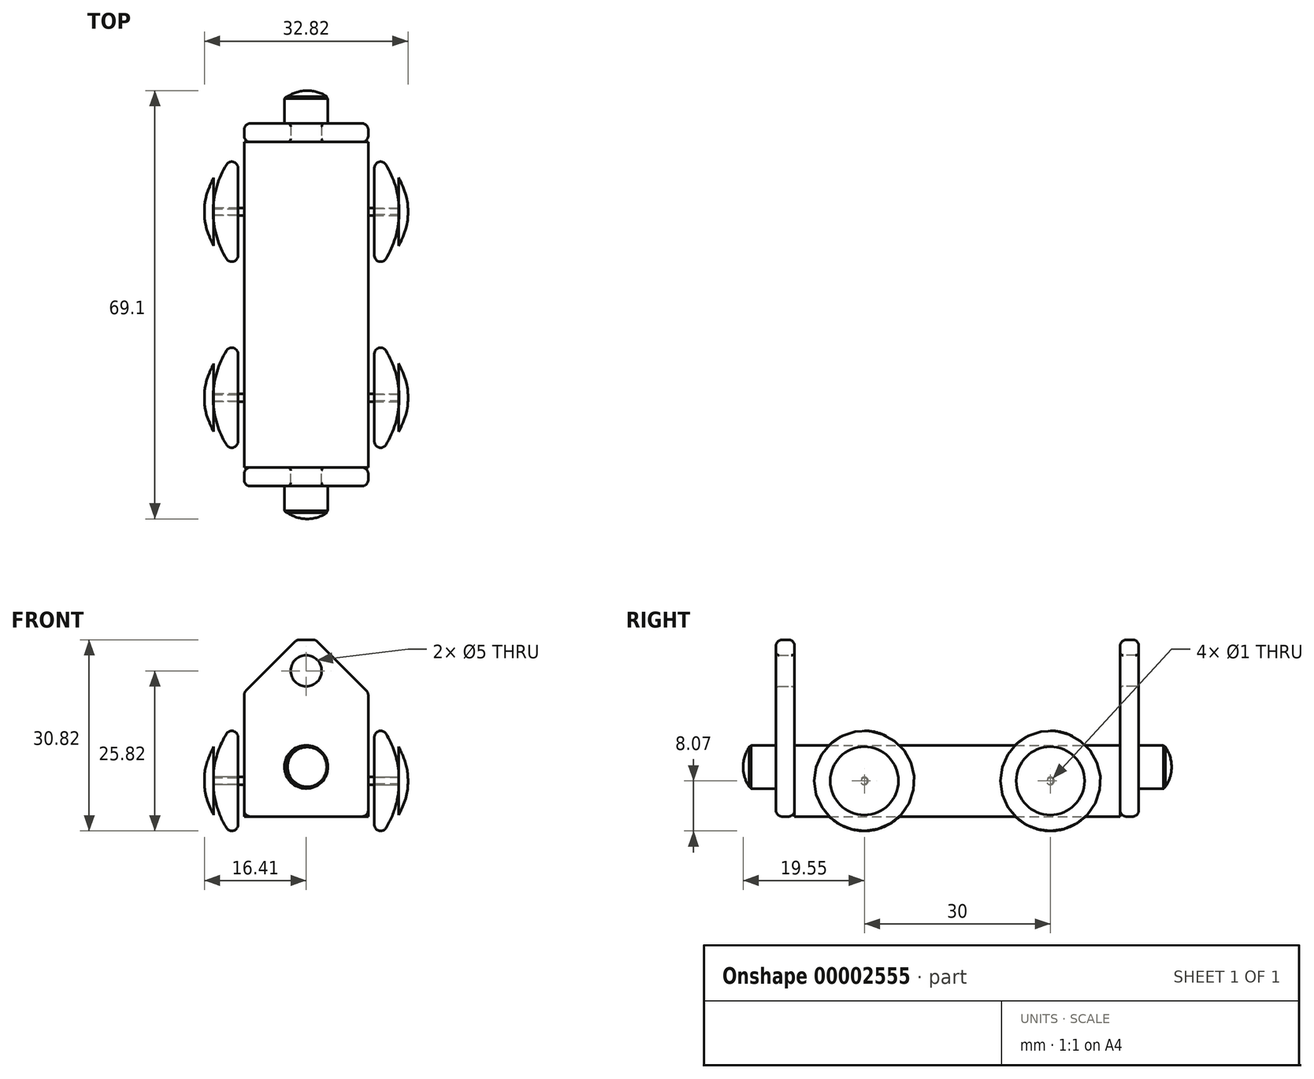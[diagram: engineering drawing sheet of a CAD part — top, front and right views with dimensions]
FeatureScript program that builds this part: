
annotation { "Feature Type Name" : "Feature", "Feature Type Description" : "" }
export const myFeature = defineFeature(function(context is Context, id is Id, definition is map)
    precondition{}
    {
        {
            var Q0;
            Q0=qCreatedBy(makeId("Top.planeOp"),FACE);
            var sketch = newSketch(context, id + "F0", { "sketchPlane" : qUnion([Q0])});
            skLineSegment(sketch, "E0.bottom", {"start": v(0, 0) * mm, "end": v(20, 0) * mm});
            skLineSegment(sketch, "E0.top", {"start": v(0, 52.5) * mm, "end": v(20, 52.5) * mm});
            skLineSegment(sketch, "E0.left", {"start": v(0, 0) * mm, "end": v(0, 52.5) * mm});
            skLineSegment(sketch, "E0.right", {"start": v(20, 0) * mm, "end": v(20, 52.5) * mm});
            skSolve(sketch);
        }
        {
            var Q0;
            Q0=makeQuery(id+"F0.imprint","IMPRINT",FACE,{"disambiguationData":[TD([[makeQuery(id+"F0.imprint","IMPRINT",EDGE,{"derivedFrom":sQuery(id+"F0.wireOp",EDGE,"E0.bottom")}),1.0]])]});
            extrude(context, id + "F1", {"entities" : qUnion([Q0]), "depth" : 11.5 * mm});
        }
        {
            var Q0;
            Q0=makeQuery(id+"F1.opExtrude","SWEPT_FACE",FACE,{"disambiguationData":[OSD([sQuery(id+"F0.wireOp",EDGE,"E0.bottom")])]});
            var sketch = newSketch(context, id + "F2", { "sketchPlane" : qUnion([Q0])});
            skLineSegment(sketch, "E1.bottom", {"start": v(1, 0) * mm, "end": v(19, 0) * mm});
            skLineSegment(sketch, "E1.top", {"start": v(0, 20) * mm, "end": v(20, 20) * mm});
            skLineSegment(sketch, "E1.left", {"start": v(0, 1) * mm, "end": v(0, 19.59) * mm});
            skLineSegment(sketch, "E1.right", {"start": v(20, 1) * mm, "end": v(20, 19.59) * mm});
            skLineSegment(sketch, "E2", {"start": v(0.3, 20.3) * mm, "end": v(8.2, 28.2) * mm});
            skLineSegment(sketch, "E3", {"start": v(8.91, 28.5) * mm, "end": v(10, 28.5) * mm});
            skLineSegment(sketch, "E4", {"start": v(10, 20) * mm, "end": v(10, 28.5) * mm, "construction": true});
            skLineSegment(sketch, "E5.0.MirrorCS", {"start": v(19.7, 20.3) * mm, "end": v(11.8, 28.2) * mm});
            skLineSegment(sketch, "E6.0.MirrorCS", {"start": v(11.09, 28.5) * mm, "end": v(10, 28.5) * mm});
            skPoint(sketch, "E7.visualSharp", {"position": v(0, 0) * mm});
            skArc(sketch, "E7.filletArc", {"start": v(0, 1) * mm, "mid": v(0.3, 0.3) * mm, "end": v(1, 0) * mm});
            skPoint(sketch, "E8.visualSharp", {"position": v(20, 0) * mm});
            skArc(sketch, "E8.filletArc", {"start": v(19, 0) * mm, "mid": v(19.7, 0.3) * mm, "end": v(20, 1) * mm});
            skPoint(sketch, "E9.visualSharp", {"position": v(20, 20) * mm});
            skArc(sketch, "E9.filletArc", {"start": v(20, 19.59) * mm, "mid": v(19.92, 19.97) * mm, "end": v(19.7, 20.3) * mm});
            skPoint(sketch, "E10.visualSharp", {"position": v(11.5, 28.5) * mm});
            skArc(sketch, "E10.filletArc", {"start": v(11.8, 28.2) * mm, "mid": v(11.47, 28.42) * mm, "end": v(11.09, 28.5) * mm});
            skPoint(sketch, "E11.visualSharp", {"position": v(8.5, 28.5) * mm});
            skArc(sketch, "E11.filletArc", {"start": v(8.91, 28.5) * mm, "mid": v(8.53, 28.42) * mm, "end": v(8.2, 28.2) * mm});
            skPoint(sketch, "E12.visualSharp", {"position": v(0, 20) * mm});
            skArc(sketch, "E12.filletArc", {"start": v(0.3, 20.3) * mm, "mid": v(0.08, 19.97) * mm, "end": v(0, 19.59) * mm});
            skCircle(sketch, "E13", {"center": v(10, 23.5) * mm, "radius": 2.5 * mm});
            skSolve(sketch);
        }
        {
            var Q0;
            {var subQ0=makeQuery(id+"F1.opExtrude","CAP_EDGE",EDGE,{"disambiguationData":[OSD([sQuery(id+"F0.wireOp",EDGE,"E0.bottom")])],"isStart":false});Q0=makeQuery(id+"F2.imprint","IMPRINT",FACE,{"disambiguationData":[TD([[makeQuery(id+"F2.imprint","IMPRINT",EDGE,{"derivedFrom":subQ0}),1.0]])]});}
            var Q1;
            Q1=makeQuery(id+"F2.imprint","IMPRINT",FACE,{"disambiguationData":[TD([[makeQuery(id+"F2.imprint","IMPRINT",EDGE,{"derivedFrom":sQuery(id+"F2.wireOp",EDGE,"E1.bottom")}),1.0]])]});
            var Q2;
            {var subQ3=sQuery(id+"F2.wireOp",EDGE,"E2");Q2=makeQuery(id+"F2.imprint","IMPRINT",FACE,{"disambiguationData":[TD([[makeQuery(id+"F2.imprint","IMPRINT",EDGE,{"derivedFrom":subQ3}),-1.0]])]});}
            extrude(context, id + "F3", {"entities" : qUnion([Q0, Q1, Q2]), "depth" : 3 * mm});
        }
        {
            var Q0;
            Q0=makeQuery(id+"F3.opExtrude","CAP_EDGE",EDGE,{"disambiguationData":[OSD([sQuery(id+"F2.wireOp",EDGE,"E2")])],"isStart":false});
            var Q1;
            Q1=makeQuery(id+"F3.opExtrude","SWEPT_FACE",FACE,{"disambiguationData":[OSD([sQuery(id+"F2.wireOp",EDGE,"E5.0.MirrorCS")])]});
            fillet(context, id + "F4", {"entities" : qUnion([Q0, Q1]), "radius" : 1 * mm, "tangentPropagation" : true, "allowEdgeOverflow" : false});
        }
        {
            var Q0;
            Q0=makeQuery(id+"F3.opExtrude","CAP_EDGE",EDGE,{"disambiguationData":[OSD([sQuery(id+"F2.wireOp",EDGE,"E13")])],"isStart":true});
            var Q1;
            Q1=makeQuery(id+"F3.opExtrude","CAP_EDGE",EDGE,{"disambiguationData":[OSD([sQuery(id+"F2.wireOp",EDGE,"E13")])],"isStart":false});
            fillet(context, id + "F5", {"entities" : qUnion([Q0, Q1]), "radius" : 0.5 * mm, "tangentPropagation" : true, "allowEdgeOverflow" : false});
        }
        {
            var Q0;
            Q0=makeQuery(id+"F1.opExtrude","SWEPT_FACE",FACE,{"disambiguationData":[OSD([sQuery(id+"F0.wireOp",EDGE,"E0.top")])]});
            var Q1;
            Q1=makeQuery(id+"F3.opExtrude","CAP_FACE",FACE,{"disambiguationData":[OSD([sQuery(id+"F2.wireOp",EDGE,"E1.bottom"),sQuery(id+"F2.wireOp",EDGE,"E1.left"),sQuery(id+"F2.wireOp",EDGE,"E1.right"),sQuery(id+"F2.wireOp",EDGE,"E2"),sQuery(id+"F2.wireOp",EDGE,"E5.0.MirrorCS"),sQuery(id+"F2.wireOp",EDGE,"E6.0.MirrorCS"),sQuery(id+"F2.wireOp",EDGE,"E7.filletArc"),sQuery(id+"F2.wireOp",EDGE,"E8.filletArc"),sQuery(id+"F2.wireOp",EDGE,"E9.filletArc"),sQuery(id+"F2.wireOp",EDGE,"E10.filletArc"),sQuery(id+"F2.wireOp",EDGE,"E11.filletArc"),sQuery(id+"F2.wireOp",EDGE,"E12.filletArc"),sQuery(id+"F2.wireOp",EDGE,"E13")])],"isStart":true});
            cPlane(context, id + "F6", {"entities" : qUnion([Q0, Q1]), "cplaneType" : CPlaneType.MID_PLANE, "offset" : 150 * mm, "width" : 150 * mm, "height" : 150 * mm});
        }
        {
            var Q0;
            Q0=makeQuery(id+"F3.opExtrude","SWEPT_BODY",BODY,{"disambiguationData":[OSD([sQuery(id+"F2.wireOp",EDGE,"E1.bottom"),sQuery(id+"F2.wireOp",EDGE,"E1.left"),sQuery(id+"F2.wireOp",EDGE,"E1.right"),sQuery(id+"F2.wireOp",EDGE,"E2"),sQuery(id+"F2.wireOp",EDGE,"E5.0.MirrorCS"),sQuery(id+"F2.wireOp",EDGE,"E6.0.MirrorCS"),sQuery(id+"F2.wireOp",EDGE,"E7.filletArc"),sQuery(id+"F2.wireOp",EDGE,"E8.filletArc"),sQuery(id+"F2.wireOp",EDGE,"E9.filletArc"),sQuery(id+"F2.wireOp",EDGE,"E10.filletArc"),sQuery(id+"F2.wireOp",EDGE,"E11.filletArc"),sQuery(id+"F2.wireOp",EDGE,"E12.filletArc"),sQuery(id+"F2.wireOp",EDGE,"E13")])]});
            var Q1;
            Q1=qCreatedBy(id+"F6.planeOp",FACE);
            mirror(context, id + "F7", {"entities" : qUnion([Q0]), "mirrorPlane" : qUnion([Q1])});
        }
        {
            var Q0;
            Q0=makeQuery(id+"F3.opExtrude","CAP_FACE",FACE,{"disambiguationData":[OSD([sQuery(id+"F2.wireOp",EDGE,"E1.bottom"),sQuery(id+"F2.wireOp",EDGE,"E1.left"),sQuery(id+"F2.wireOp",EDGE,"E1.right"),sQuery(id+"F2.wireOp",EDGE,"E2"),sQuery(id+"F2.wireOp",EDGE,"E5.0.MirrorCS"),sQuery(id+"F2.wireOp",EDGE,"E6.0.MirrorCS"),sQuery(id+"F2.wireOp",EDGE,"E7.filletArc"),sQuery(id+"F2.wireOp",EDGE,"E8.filletArc"),sQuery(id+"F2.wireOp",EDGE,"E9.filletArc"),sQuery(id+"F2.wireOp",EDGE,"E10.filletArc"),sQuery(id+"F2.wireOp",EDGE,"E11.filletArc"),sQuery(id+"F2.wireOp",EDGE,"E12.filletArc"),sQuery(id+"F2.wireOp",EDGE,"E13")])],"isStart":false});
            var sketch = newSketch(context, id + "F8", { "sketchPlane" : qUnion([Q0])});
            skLineSegment(sketch, "E14", {"start": v(10, 1) * mm, "end": v(10, 8) * mm, "construction": true});
            skCircle(sketch, "E15", {"center": v(10, 8) * mm, "radius": 3.5 * mm});
            skSolve(sketch);
        }
        {
            var Q0;
            Q0=makeQuery(id+"F8.imprint","IMPRINT",FACE,{"disambiguationData":[TD([[makeQuery(id+"F8.imprint","IMPRINT",EDGE,{"derivedFrom":sQuery(id+"F8.wireOp",EDGE,"E15")}),1.0]])]});
            extrude(context, id + "F9", {"entities" : qUnion([Q0]), "depth" : 4.3 * mm});
        }
        {
            var Q0;
            Q0=makeQuery(id+"F9.opExtrude","CAP_FACE",FACE,{"disambiguationData":[OSD([sQuery(id+"F8.wireOp",EDGE,"E15")])],"isStart":false});
            chamfer(context, id + "F10", {"entities" : qUnion([Q0]), "width" : 0.3 * mm, "tangentPropagation" : true});
        }
        {
            var Q0;
            Q0=makeQuery(id+"F9.opExtrude","CAP_FACE",FACE,{"disambiguationData":[OSD([sQuery(id+"F8.wireOp",EDGE,"E15")])],"isStart":false});
            var sketch = newSketch(context, id + "F11", { "sketchPlane" : qUnion([Q0])});
            skLineSegment(sketch, "E16", {"start": v(10.17, 11.2) * mm, "end": v(10.17, 4.8) * mm, "construction": true});
            skSolve(sketch);
        }
        {
            var Q0;
            Q0=sQuery(id+"F11.wireOp",EDGE,"E16");
            cPlane(context, id + "F12", {"entities" : qUnion([Q0]), "cplaneType" : CPlaneType.LINE_ANGLE, "offset" : 150 * mm, "angle" : 0 * degree, "width" : 150 * mm, "height" : 150 * mm});
        }
        {
            var Q0;
            Q0=qCreatedBy(id+"F12.planeOp",FACE);
            var sketch = newSketch(context, id + "F13", { "sketchPlane" : qUnion([Q0])});
            skArc(sketch, "E17", {"start": v(8.3, 8) * mm, "mid": v(8.04, 9.67) * mm, "end": v(7.3, 11.2) * mm});
            skPoint(sketch, "E17.first.point", {"position": v(7.3, 11.2) * mm});
            skPoint(sketch, "E17.second.point", {"position": v(7.3, 4.8) * mm});
            skPoint(sketch, "E17.third.point", {"position": v(-2.88, 7.11) * mm});
            skLineSegment(sketch, "E18.0", {"start": v(7.3, 11.2) * mm, "end": v(7.3, 4.8) * mm});
            skLineSegment(sketch, "E19", {"start": v(8.3, 8) * mm, "end": v(7.3, 8) * mm});
            skSolve(sketch);
        }
        {
            var Q0;
            {var subQ2=sQuery(id+"F13.wireOp",EDGE,"E17");Q0=makeQuery(id+"F13.imprint","IMPRINT",FACE,{"disambiguationData":[TD([[makeQuery(id+"F13.imprint","IMPRINT",EDGE,{"derivedFrom":subQ2}),1.0]])]});}
            var Q1;
            Q1=sQuery(id+"F13.wireOp",EDGE,"E19");
            revolve(context, id + "F14", {"entities" : qUnion([Q0]), "axis" : qUnion([Q1]), "revolveType" : RevolveType.FULL});
        }
        {
            var Q0;
            Q0=makeQuery(id+"F9.opExtrude","SWEPT_BODY",BODY,{"disambiguationData":[OSD([sQuery(id+"F8.wireOp",EDGE,"E15")])]});
            var Q1;
            Q1=makeQuery(id+"F14.opRevolve","SWEPT_BODY",BODY,{"disambiguationData":[OSD([sQuery(id+"F13.wireOp",EDGE,"E17"),sQuery(id+"F13.wireOp",EDGE,"E18.0"),sQuery(id+"F13.wireOp",EDGE,"E19")])]});
            var Q2;
            Q2=qCreatedBy(id+"F6.planeOp",FACE);
            mirror(context, id + "F15", {"entities" : qUnion([Q0, Q1]), "mirrorPlane" : qUnion([Q2])});
        }
        {
            var Q0;
            Q0=qCreatedBy(id+"F6.planeOp",FACE);
            var sketch = newSketch(context, id + "F16", { "sketchPlane" : qUnion([Q0])});
            skArc(sketch, "E20", {"start": v(2.85, -1.84) * mm, "mid": v(4.45, 1.8) * mm, "end": v(5, 5.75) * mm});
            skPoint(sketch, "E20.first.point", {"position": v(1, 15.75) * mm});
            skPoint(sketch, "E20.second.point", {"position": v(1, -4.25) * mm});
            skLineSegment(sketch, "E21.0", {"start": v(0, 11.5) * mm, "end": v(0, 0) * mm, "construction": true});
            skLineSegment(sketch, "E22", {"start": v(0, 5.75) * mm, "end": v(-31.51, 5.75) * mm, "construction": true});
            skLineSegment(sketch, "E23", {"start": v(1, 5.75) * mm, "end": v(1, -1.32) * mm});
            skArc(sketch, "E24.filletArc", {"start": v(1, -1.32) * mm, "mid": v(1.73, -2.28) * mm, "end": v(2.85, -1.84) * mm});
            skLineSegment(sketch, "E25", {"start": v(1, 5.75) * mm, "end": v(5, 5.75) * mm, "construction": true});
            skLineSegment(sketch, "E26", {"start": v(1, 5.25) * mm, "end": v(5, 5.25) * mm});
            skSolve(sketch);
        }
        {
            var Q0;
            Q0=qCreatedBy(id+"F6.planeOp",FACE);
            cPlane(context, id + "F17", {"entities" : qUnion([Q0]), "cplaneType" : CPlaneType.OFFSET, "offset" : 15 * mm, "width" : 150 * mm, "height" : 150 * mm});
        }
        {
            var Q0;
            Q0=qCreatedBy(id+"F17.planeOp",FACE);
            var sketch = newSketch(context, id + "F18", { "sketchPlane" : qUnion([Q0])});
            skLineSegment(sketch, "E27.0", {"start": v(1, 5.75) * mm, "end": v(1, -1.32) * mm});
            skArc(sketch, "E28.0", {"start": v(1, -1.32) * mm, "mid": v(1.73, -2.28) * mm, "end": v(2.85, -1.84) * mm});
            skArc(sketch, "E29.0", {"start": v(2.85, -1.84) * mm, "mid": v(4.45, 1.8) * mm, "end": v(5, 5.75) * mm});
            skLineSegment(sketch, "E30.0", {"start": v(1, 5.25) * mm, "end": v(5, 5.25) * mm});
            skLineSegment(sketch, "E31.0", {"start": v(1, 5.75) * mm, "end": v(5, 5.75) * mm, "construction": true});
            skSolve(sketch);
        }
        {
            var Q0;
            {var subQ2=sQuery(id+"F18.wireOp",EDGE,"E28.0");Q0=makeQuery(id+"F18.imprint","IMPRINT",FACE,{"disambiguationData":[TD([[makeQuery(id+"F18.imprint","IMPRINT",EDGE,{"derivedFrom":subQ2}),1.0]])]});}
            var Q1;
            Q1=sQuery(id+"F18.wireOp",EDGE,"E31.0");
            revolve(context, id + "F19", {"entities" : qUnion([Q0]), "axis" : qUnion([Q1]), "revolveType" : RevolveType.FULL});
        }
        {
            var Q0;
            Q0=qCreatedBy(id+"F17.planeOp",FACE);
            var sketch = newSketch(context, id + "F20", { "sketchPlane" : qUnion([Q0])});
            skLineSegment(sketch, "E32", {"start": v(0, 5.13) * mm, "end": v(4.91, 5.13) * mm});
            skLineSegment(sketch, "E33", {"start": v(4.91, 5.13) * mm, "end": v(4.91, 0.25) * mm});
            skFitSpline(sketch, "E34", {"points": [v(4.91, 0.25) * mm, v(6.17, 3.4) * mm, v(6.4, 5.75) * mm], "startDerivative": vector(0.77, 1.16) * mm, "endDerivative": vector(0.03, 2.6) * mm});
            skLineSegment(sketch, "E35.0", {"start": v(1, 5.75) * mm, "end": v(6.4, 5.75) * mm, "construction": true});
            skPoint(sketch, "E36.orphan", {"position": v(5, 5.75) * mm});
            skLineSegment(sketch, "E37", {"start": v(6.4, 5.75) * mm, "end": v(0, 5.75) * mm});
            skLineSegment(sketch, "E38", {"start": v(0, 5.75) * mm, "end": v(0, 5.13) * mm});
            skSolve(sketch);
        }
        {
            var Q0;
            Q0=makeQuery(id+"F20.imprint","IMPRINT",FACE,{"disambiguationData":[TD([[makeQuery(id+"F20.imprint","IMPRINT",EDGE,{"derivedFrom":sQuery(id+"F20.wireOp",EDGE,"E32")}),1.0]])]});
            var Q1;
            Q1=sQuery(id+"F20.wireOp",EDGE,"E37");
            revolve(context, id + "F21", {"entities" : qUnion([Q0]), "axis" : qUnion([Q1]), "revolveType" : RevolveType.FULL});
        }
        {
            var Q0;
            Q0=makeQuery(id+"F21.opRevolve","SWEPT_BODY",BODY,{"disambiguationData":[OSD([sQuery(id+"F20.wireOp",EDGE,"E32"),sQuery(id+"F20.wireOp",EDGE,"E33"),sQuery(id+"F20.wireOp",EDGE,"E34"),sQuery(id+"F20.wireOp",EDGE,"E37"),sQuery(id+"F20.wireOp",EDGE,"E38")])]});
            var Q1;
            Q1=makeQuery(id+"F19.opRevolve","SWEPT_BODY",BODY,{"disambiguationData":[OSD([sQuery(id+"F18.wireOp",EDGE,"E27.0"),sQuery(id+"F18.wireOp",EDGE,"E28.0"),sQuery(id+"F18.wireOp",EDGE,"E29.0"),sQuery(id+"F18.wireOp",EDGE,"E30.0")])]});
            var Q2;
            Q2=qCreatedBy(id+"F6.planeOp",FACE);
            mirror(context, id + "F22", {"entities" : qUnion([Q0, Q1]), "mirrorPlane" : qUnion([Q2])});
        }
        {
            var Q0;
            Q0=makeQuery(id+"F1.opExtrude","SWEPT_FACE",FACE,{"disambiguationData":[OSD([sQuery(id+"F0.wireOp",EDGE,"E0.left")])]});
            var Q1;
            Q1=makeQuery(id+"F1.opExtrude","SWEPT_FACE",FACE,{"disambiguationData":[OSD([sQuery(id+"F0.wireOp",EDGE,"E0.right")])]});
            cPlane(context, id + "F23", {"entities" : qUnion([Q0, Q1]), "cplaneType" : CPlaneType.MID_PLANE, "offset" : 150 * mm, "width" : 150 * mm, "height" : 150 * mm});
        }
        {
            var Q0;
            Q0=makeQuery(id+"F22.opPattern","COPY",BODY,{"derivedFrom":makeQuery(id+"F21.opRevolve","SWEPT_BODY",BODY,{"disambiguationData":[OSD([sQuery(id+"F20.wireOp",EDGE,"E32"),sQuery(id+"F20.wireOp",EDGE,"E33"),sQuery(id+"F20.wireOp",EDGE,"E34"),sQuery(id+"F20.wireOp",EDGE,"E37"),sQuery(id+"F20.wireOp",EDGE,"E38")])]}),"instanceName":"1"});
            var Q1;
            Q1=makeQuery(id+"F19.opRevolve","SWEPT_BODY",BODY,{"disambiguationData":[OSD([sQuery(id+"F18.wireOp",EDGE,"E27.0"),sQuery(id+"F18.wireOp",EDGE,"E28.0"),sQuery(id+"F18.wireOp",EDGE,"E29.0"),sQuery(id+"F18.wireOp",EDGE,"E30.0")])]});
            var Q2;
            Q2=makeQuery(id+"F22.opPattern","COPY",BODY,{"derivedFrom":makeQuery(id+"F19.opRevolve","SWEPT_BODY",BODY,{"disambiguationData":[OSD([sQuery(id+"F18.wireOp",EDGE,"E27.0"),sQuery(id+"F18.wireOp",EDGE,"E28.0"),sQuery(id+"F18.wireOp",EDGE,"E29.0"),sQuery(id+"F18.wireOp",EDGE,"E30.0")])]}),"instanceName":"1"});
            var Q3;
            Q3=makeQuery(id+"F21.opRevolve","SWEPT_BODY",BODY,{"disambiguationData":[OSD([sQuery(id+"F20.wireOp",EDGE,"E32"),sQuery(id+"F20.wireOp",EDGE,"E33"),sQuery(id+"F20.wireOp",EDGE,"E34"),sQuery(id+"F20.wireOp",EDGE,"E37"),sQuery(id+"F20.wireOp",EDGE,"E38")])]});
            var Q4;
            Q4=qCreatedBy(id+"F23.planeOp",FACE);
            mirror(context, id + "F24", {"entities" : qUnion([Q0, Q1, Q2, Q3]), "mirrorPlane" : qUnion([Q4])});
        }
    });
